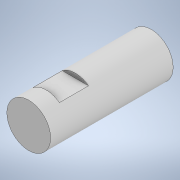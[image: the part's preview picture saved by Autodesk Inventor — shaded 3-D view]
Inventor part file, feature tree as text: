
AUTODESK INVENTOR PART (.ipt)
format: ipt  version: 2021 (Build 250183000, 183)  size: 100,352 bytes
history: native  units: in
note: dims shown in document units (in); Inventor stores cm internally (conversion verified against a paired STEP export)
features: extrude x2, sketch x2, other x1, plane x1
ambient origin geometry x8: Origin, YZ Plane, XZ Plane, XY Plane, X Axis, Y Axis, Z Axis, Center Point
bodies: Body1 (feature_tree)
feature tree (6):
  other  "Sólido1"
  extrude  "Extrusión1"  Depth=1.6535in TaperAngle=0.0deg
  plane  "Plano de trabajo1"
  extrude  "Extrusión2"  Depth=0.3937in
  sketch  "Boceto1"  dims[d0=0.5906in d1=1.6535in d2=0.0in]
  sketch  "Boceto3"  dims[d3=0.1969in d4=0.0591in d5=0.3937in d6=0.0in]
